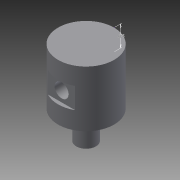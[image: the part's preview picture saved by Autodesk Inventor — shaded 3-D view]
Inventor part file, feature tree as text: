
AUTODESK INVENTOR PART (.ipt)
format: ipt  version: 2014 SP1 (Build 180222100, 222)  size: 103,936 bytes
history: native  units: in
note: dims shown in document units (in); Inventor stores cm internally (conversion verified against a paired STEP export)
features: sketch x4, extrude x2, revolve x1, projected_geometry x1
ambient origin geometry x8: Origin, YZ Plane, XZ Plane, XY Plane, X Axis, Y Axis, Z Axis, Center Point
bodies: Solid1 (feature_tree)
feature tree (8):
  revolve  "Revolution1"  [1 undecoded]
  extrude  "Extrusion1"  Depth=1.0in
  extrude  "Extrusion2"  Depth=0.25in
  sketch  "Sketch4"  dims[d6=1.0in d7=0.0in d9=0.0625in d10=0.0625in d11=0.375in d12=1.0in d13=0.0in d14=0.375in]
  sketch  "Sketch1"  dims[d0=1.5in d1=0.5in]
  sketch  "Sketch2"  dims[d2=1.0in d3=0.325in]
  sketch  "Sketch3"  dims[d4=90.0deg d5=0.25in]
  projected_geometry  "Project Cut Edges1"
note: 1 required parameter value undecoded (feature->parameter linkage not recoverable at this tier; creation-order binding heuristic only, values carry confidence <= 0.55)
